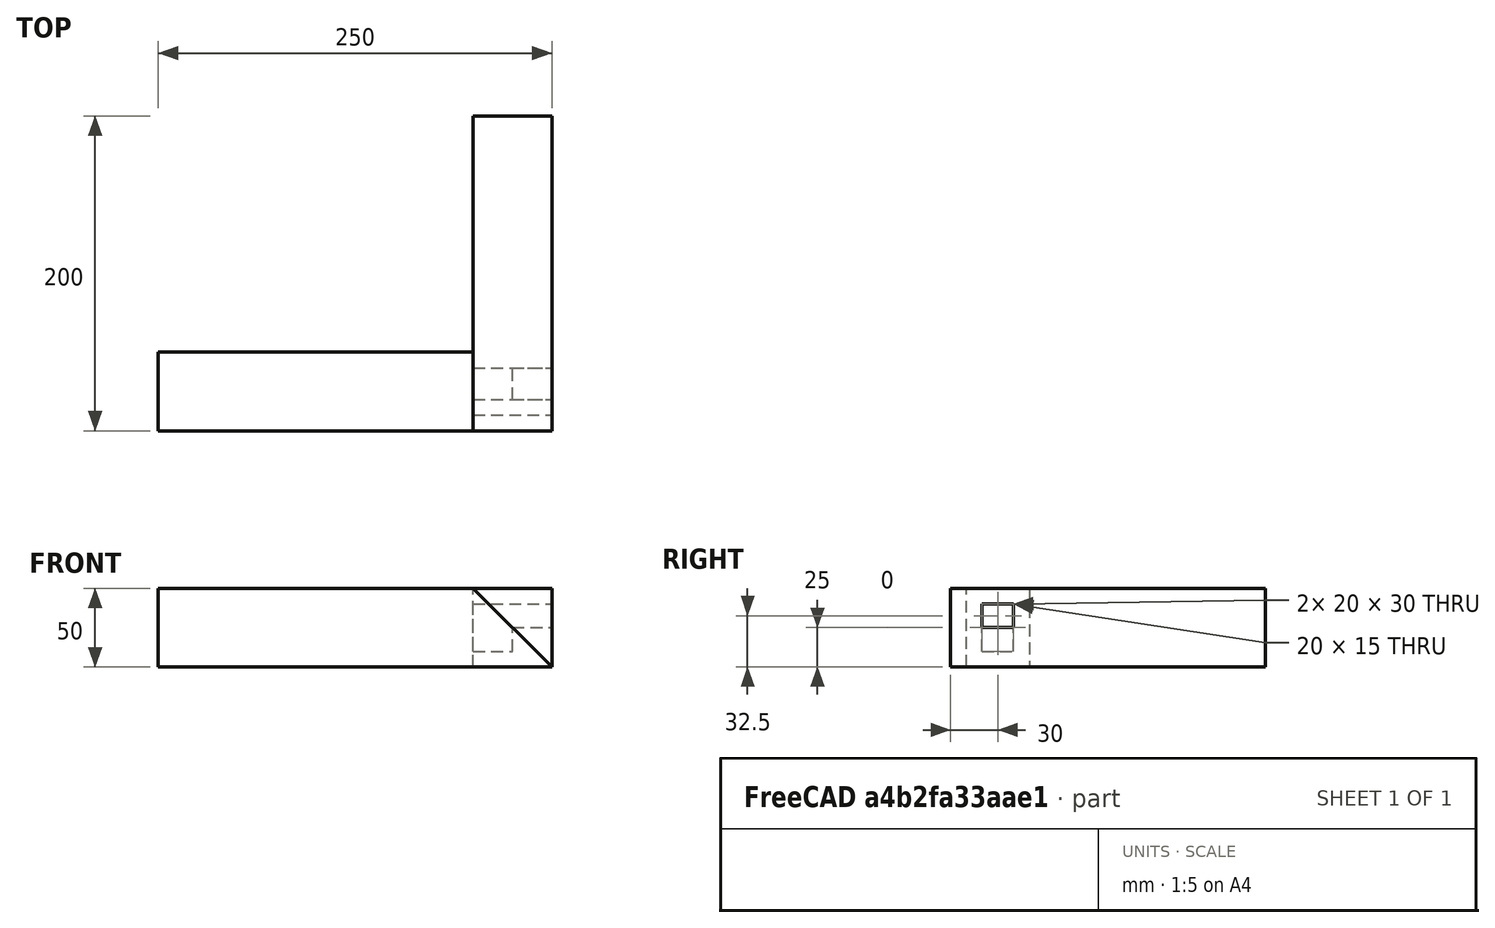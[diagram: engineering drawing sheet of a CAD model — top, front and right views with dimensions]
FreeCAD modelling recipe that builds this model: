
FCSTD DOCUMENT  (FreeCAD 0.19R16207 (Git))
Label: EMENDA L
License: All rights reserved
LicenseURL: http://en.wikipedia.org/wiki/All_rights_reserved
objects: Part::Box×6, Part::Cut×3, Part::Feature×3, Part::MultiFuse×1
note: 13 computed .brp shape members not serialized (recipe doc carries the construction recipe); baked Part::Feature solids carry a one-line shape summary decoded from their .brp

FEATURE [Part::Box] Box  label="Cube"
  AttacherType = Attacher::AttachEngine3D
  Height = 50
  Length = 50
  Width = 10
FEATURE [Part::Box] Box001  label="Cube001"
  AttacherType = Attacher::AttachEngine3D
  Height = 100
  Length = 100
  Placement = pos=(0,0,50) rot=(0,1,0;0.785398rad)
  Width = 10
FEATURE [Part::Cut] Cut
  Base = -> Box
  Tool = -> Box001
FEATURE [Part::Box] Box002  label="Cube002"
  AttacherType = Attacher::AttachEngine3D
  Height = 50
  Length = 200
  Placement = pos=(-6.1e-15,0,50) rot=(0,1,0;3.14159rad)
  Width = 50
FEATURE [Part::Box] Box003  label="Cube003"
  AttacherType = Attacher::AttachEngine3D
  Height = 30
  Length = 50
  Placement = pos=(0,20,10) rot=(0,0,1;0rad)
  Width = 20
FEATURE [Part::Box] Box004  label="Cube004"
  AttacherType = Attacher::AttachEngine3D
  Height = 20
  Length = 25
  Placement = pos=(25,20,5) rot=(0,0,1;0rad)
  Width = 20
FEATURE [Part::MultiFuse] Fusion
  Shapes = -> [Cut,Box002,Box003]
FEATURE [Part::Cut] Cut001
  Base = -> Fusion
  Tool = -> Box004
FEATURE [Part::Feature] Cut001001  label="Cut002"
  shape: bbox 250 x 50 x 50 mm, 15 faces (baked)
FEATURE [Part::Box] Box005  label="Cube005"
  AttacherType = Attacher::AttachEngine3D
  Height = 50
  Length = 50
  Width = 200
FEATURE [Part::Cut] Cut001002
  Base = -> Box005
  Tool = -> Cut001001
FEATURE [Part::Feature] Cut001002001  label="Cut001003"
  shape: bbox 50 x 200 x 50 mm, 14 faces (baked)
FEATURE [Part::Feature] Cut001002002  label="Cut001004"
  shape: bbox 250 x 50 x 50 mm, 15 faces (baked)
